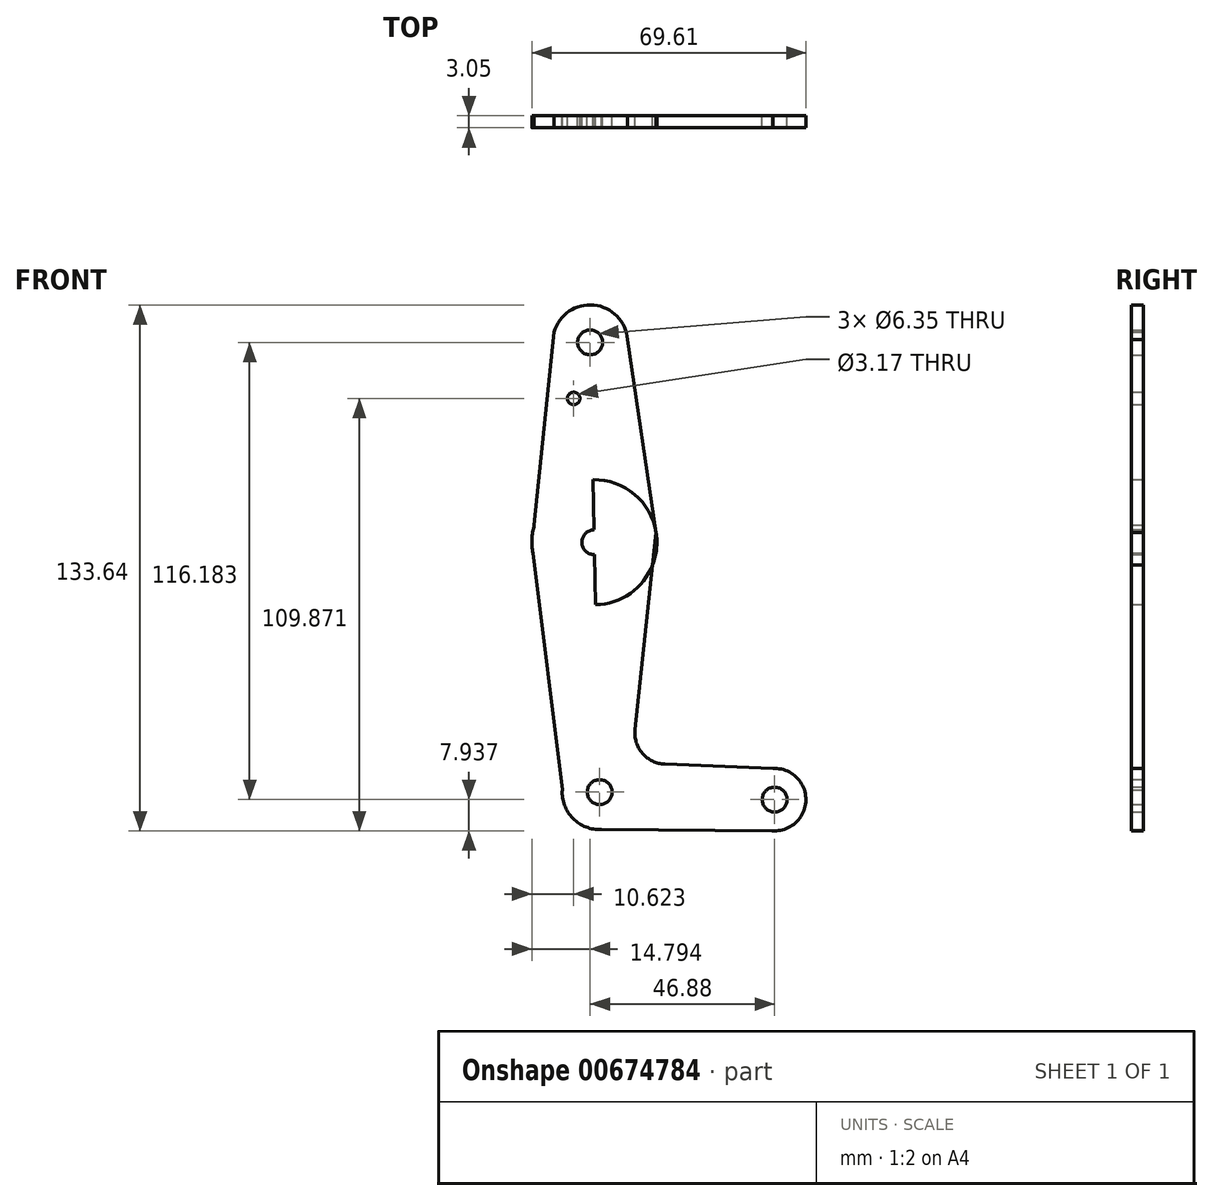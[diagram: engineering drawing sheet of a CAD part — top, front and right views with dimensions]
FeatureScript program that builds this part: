
annotation { "Feature Type Name" : "Feature", "Feature Type Description" : "" }
export const myFeature = defineFeature(function(context is Context, id is Id, definition is map)
    precondition{}
    {
        {
            var Q0;
            Q0=qCreatedBy(makeId("Front.planeOp"),FACE);
            var sketch = newSketch(context, id + "F0", { "sketchPlane" : qUnion([Q0])});
            skLineSegment(sketch, "E0", {"start": v(-15.57, 58.35) * mm, "end": v(-13.14, -55.92) * mm});
            skLineSegment(sketch, "E1", {"start": v(-13.14, -55.92) * mm, "end": v(31.31, -57.83) * mm});
            skCircle(sketch, "E2", {"center": v(-15.57, 58.35) * mm, "radius": 9.53 * mm});
            skCircle(sketch, "E3", {"center": v(-14.49, 7.58) * mm, "radius": 15.88 * mm});
            skCircle(sketch, "E4", {"center": v(-13.14, -55.92) * mm, "radius": 9.53 * mm});
            skCircle(sketch, "E5", {"center": v(31.31, -57.83) * mm, "radius": 7.94 * mm});
            skLineSegment(sketch, "E6", {"start": v(-24.73, 60.95) * mm, "end": v(-30.32, 6.45) * mm});
            skLineSegment(sketch, "E7", {"start": v(-30.32, 6.45) * mm, "end": v(-22.64, -55.36) * mm});
            skLineSegment(sketch, "E8", {"start": v(-6.07, 59.04) * mm, "end": v(1.2, 10.04) * mm});
            skLineSegment(sketch, "E9", {"start": v(1.2, 10.04) * mm, "end": v(-4.17, -40.03) * mm});
            skLineSegment(sketch, "E10", {"start": v(3.42, -48.82) * mm, "end": v(30.82, -49.91) * mm});
            skLineSegment(sketch, "E11", {"start": v(-12.73, -65.44) * mm, "end": v(31.9, -65.75) * mm});
            skCircle(sketch, "E12", {"center": v(-15.57, 58.35) * mm, "radius": 3.18 * mm});
            skCircle(sketch, "E13", {"center": v(-14.49, 7.58) * mm, "radius": 3.18 * mm});
            skCircle(sketch, "E14", {"center": v(-13.14, -55.92) * mm, "radius": 3.18 * mm});
            skCircle(sketch, "E15", {"center": v(31.31, -57.83) * mm, "radius": 3.18 * mm});
            skCircle(sketch, "E16", {"center": v(-19.74, 44.1) * mm, "radius": 1.59 * mm});
            skArc(sketch, "E17.filletArc", {"start": v(-4.17, -40.03) * mm, "mid": v(-2.28, -46.07) * mm, "end": v(3.42, -48.82) * mm});
            skSolve(sketch);
        }
        {
            var Q0;
            {var subQ0=sQuery(id+"F0.wireOp",EDGE,"E6");var subQ1=sQuery(id+"F0.wireOp",EDGE,"E2");var subQ2=makeQuery(id+"F0.imprint","INTERSECT",VERTEX,{"disambiguationData":[OD(0.0)],"derivedFrom":[subQ1,subQ0]});Q0=makeQuery(id+"F0.imprint","IMPRINT",FACE,{"disambiguationData":[TD([[makeQuery(id+"F0.imprint","IMPRINT",EDGE,{"disambiguationData":[TD([[subQ2,-1.0]])],"derivedFrom":subQ1}),1.0]])]});}
            var Q1;
            {var subQ0=sQuery(id+"F0.wireOp",EDGE,"E9");var subQ1=sQuery(id+"F0.wireOp",EDGE,"E3");var subQ3=makeQuery(id+"F0.imprint","INTERSECT",VERTEX,{"derivedFrom":[subQ1,subQ0]});Q1=makeQuery(id+"F0.imprint","IMPRINT",FACE,{"disambiguationData":[TD([[makeQuery(id+"F0.imprint","IMPRINT",EDGE,{"disambiguationData":[TD([[subQ3,-1.0]])],"derivedFrom":subQ1}),1.0]])]});}
            var Q2;
            Q2=makeQuery(id+"F0.imprint","IMPRINT",FACE,{"disambiguationData":[TD([[makeQuery(id+"F0.imprint","IMPRINT",EDGE,{"derivedFrom":sQuery(id+"F0.wireOp",EDGE,"E12")}),-1.0]])]});
            var Q3;
            {var subQ0=sQuery(id+"F0.wireOp",EDGE,"E11");var subQ1=sQuery(id+"F0.wireOp",EDGE,"E5");var subQ2=makeQuery(id+"F0.imprint","INTERSECT",VERTEX,{"disambiguationData":[OD(0.0)],"derivedFrom":[subQ1,subQ0]});Q3=makeQuery(id+"F0.imprint","IMPRINT",FACE,{"disambiguationData":[TD([[makeQuery(id+"F0.imprint","IMPRINT",EDGE,{"disambiguationData":[TD([[subQ2,1.0]])],"derivedFrom":subQ1}),1.0]])]});}
            var Q4;
            {var subQ1=sQuery(id+"F0.wireOp",EDGE,"E3");var subQ3=sQuery(id+"F0.wireOp",EDGE,"E0");var subQ4=makeQuery(id+"F0.imprint","INTERSECT",VERTEX,{"disambiguationData":[OD(0.0)],"derivedFrom":[subQ3,subQ1]});Q4=makeQuery(id+"F0.imprint","IMPRINT",FACE,{"disambiguationData":[TD([[makeQuery(id+"F0.imprint","IMPRINT",EDGE,{"disambiguationData":[TD([[subQ4,-1.0]])],"derivedFrom":subQ3}),-1.0]])]});}
            var Q5;
            Q5=makeQuery(id+"F0.imprint","IMPRINT",FACE,{"disambiguationData":[TD([[makeQuery(id+"F0.imprint","IMPRINT",EDGE,{"derivedFrom":sQuery(id+"F0.wireOp",EDGE,"E15")}),-1.0]])]});
            var Q6;
            {var subQ0=sQuery(id+"F0.wireOp",EDGE,"E5");var subQ1=sQuery(id+"F0.wireOp",EDGE,"E1");var subQ2=makeQuery(id+"F0.imprint","INTERSECT",VERTEX,{"derivedFrom":[subQ1,subQ0]});Q6=makeQuery(id+"F0.imprint","IMPRINT",FACE,{"disambiguationData":[TD([[makeQuery(id+"F0.imprint","IMPRINT",EDGE,{"disambiguationData":[TD([[subQ2,1.0]])],"derivedFrom":subQ1}),-1.0]])]});}
            var Q7;
            {var subQ0=sQuery(id+"F0.wireOp",EDGE,"E4");var subQ3=sQuery(id+"F0.wireOp",EDGE,"E0");var subQ4=makeQuery(id+"F0.imprint","INTERSECT",VERTEX,{"derivedFrom":[subQ3,subQ0]});Q7=makeQuery(id+"F0.imprint","IMPRINT",FACE,{"disambiguationData":[TD([[makeQuery(id+"F0.imprint","IMPRINT",EDGE,{"disambiguationData":[TD([[subQ4,-1.0]])],"derivedFrom":subQ3}),-1.0]])]});}
            var Q8;
            {var subQ0=sQuery(id+"F0.wireOp",EDGE,"E6");var subQ1=sQuery(id+"F0.wireOp",EDGE,"E3");var subQ3=makeQuery(id+"F0.imprint","INTERSECT",VERTEX,{"derivedFrom":[subQ1,subQ0]});Q8=makeQuery(id+"F0.imprint","IMPRINT",FACE,{"disambiguationData":[TD([[makeQuery(id+"F0.imprint","IMPRINT",EDGE,{"disambiguationData":[TD([[subQ3,-1.0]])],"derivedFrom":subQ1}),1.0]])]});}
            var Q9;
            {var subQ1=sQuery(id+"F0.wireOp",EDGE,"E3");var subQ3=sQuery(id+"F0.wireOp",EDGE,"E0");var subQ6=makeQuery(id+"F0.imprint","INTERSECT",VERTEX,{"disambiguationData":[OD(0.0)],"derivedFrom":[subQ3,subQ1]});Q9=makeQuery(id+"F0.imprint","IMPRINT",FACE,{"disambiguationData":[TD([[makeQuery(id+"F0.imprint","IMPRINT",EDGE,{"disambiguationData":[TD([[subQ6,-1.0]])],"derivedFrom":subQ3}),1.0]])]});}
            var Q10;
            Q10=makeQuery(id+"F0.imprint","IMPRINT",FACE,{"disambiguationData":[TD([[makeQuery(id+"F0.imprint","IMPRINT",EDGE,{"derivedFrom":sQuery(id+"F0.wireOp",EDGE,"E16")}),-1.0]])]});
            var Q11;
            {var subQ5=sQuery(id+"F0.wireOp",EDGE,"E8");Q11=makeQuery(id+"F0.imprint","IMPRINT",FACE,{"disambiguationData":[TD([[makeQuery(id+"F0.imprint","IMPRINT",EDGE,{"derivedFrom":subQ5}),-1.0]])]});}
            var Q12;
            {var subQ0=sQuery(id+"F0.wireOp",EDGE,"E7");var subQ1=sQuery(id+"F0.wireOp",EDGE,"E3");var subQ3=makeQuery(id+"F0.imprint","INTERSECT",VERTEX,{"derivedFrom":[subQ1,subQ0]});Q12=makeQuery(id+"F0.imprint","IMPRINT",FACE,{"disambiguationData":[TD([[makeQuery(id+"F0.imprint","IMPRINT",EDGE,{"disambiguationData":[TD([[subQ3,1.0]])],"derivedFrom":subQ1}),1.0]])]});}
            var Q13;
            {var subQ0=sQuery(id+"F0.wireOp",EDGE,"E3");var subQ1=sQuery(id+"F0.wireOp",EDGE,"E0");var subQ2=makeQuery(id+"F0.imprint","INTERSECT",VERTEX,{"disambiguationData":[OD(1.0)],"derivedFrom":[subQ1,subQ0]});Q13=makeQuery(id+"F0.imprint","IMPRINT",FACE,{"disambiguationData":[TD([[makeQuery(id+"F0.imprint","IMPRINT",EDGE,{"disambiguationData":[TD([[subQ2,-1.0]])],"derivedFrom":subQ1}),-1.0]])]});}
            var Q14;
            {var subQ0=sQuery(id+"F0.wireOp",EDGE,"E4");var subQ1=sQuery(id+"F0.wireOp",EDGE,"E0");var subQ2=makeQuery(id+"F0.imprint","INTERSECT",VERTEX,{"derivedFrom":[subQ1,subQ0]});Q14=makeQuery(id+"F0.imprint","IMPRINT",FACE,{"disambiguationData":[TD([[makeQuery(id+"F0.imprint","IMPRINT",EDGE,{"disambiguationData":[TD([[subQ2,-1.0]])],"derivedFrom":subQ1}),1.0]])]});}
            var Q15;
            {var subQ11=sQuery(id+"F0.wireOp",EDGE,"E10");Q15=makeQuery(id+"F0.imprint","IMPRINT",FACE,{"disambiguationData":[TD([[makeQuery(id+"F0.imprint","IMPRINT",EDGE,{"derivedFrom":subQ11}),-1.0]])]});}
            extrude(context, id + "F1", {"entities" : qUnion([Q0, Q1, Q2, Q3, Q4, Q5, Q6, Q7, Q8, Q9, Q10, Q11, Q12, Q13, Q14, Q15]), "depth" : 3.05 * mm, "offsetDistance" : 25.4 * mm});
        }
    });
